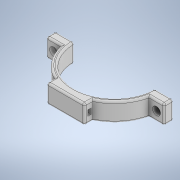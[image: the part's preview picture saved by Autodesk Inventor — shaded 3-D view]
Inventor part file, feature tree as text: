
AUTODESK INVENTOR PART (.ipt)
format: ipt  version: 2020 (Build 240168000, 168)  size: 262,656 bytes
history: native  units: in
note: dims shown in document units (in); Inventor stores cm internally (conversion verified against a paired STEP export)
features: sketch x6, extrude x5, plane x2, mirror x2, shell x1, hole x1, fillet x1, chamfer x1
ambient origin geometry x8: Origin, YZ Plane, XZ Plane, XY Plane, X Axis, Y Axis, Z Axis, Center Point
bodies: Solid1 (feature_tree)
feature tree (19):
  extrude  "Extrusion1"  Depth=0.1969in TaperAngle=0.0deg
  shell  "Shell1"  Thickness=0.1969in
  extrude  "Extrusion2"  [1 undecoded]
  plane  "Work Plane1"
  extrude  "Extrusion3"  Depth=0.3937in
  mirror  "Mirror1"
  hole  "Hole2"  [1 undecoded]
  mirror  "Mirror2"
  plane  "Work Plane2"
  extrude  "Extrusion4"  Depth=0.0984in TaperAngle=0.0deg
  fillet  "Fillet1"  Radius=0.0787in
  extrude  "Extrusion6"  Depth=0.0984in
  chamfer  "Chamfer2"  Distance=0.1969in
  sketch  "Sketch1"  dims[d0=3.7402in d1=0.7874in d2=0.0in d3=0.1969in]
  sketch  "Sketch2"  dims[d4=0.3937in d5=0.0in d6=-1.8701in]
  sketch  "Sketch3"  dims[d7=0.7874in d8=0.3937in]
  sketch  "Sketch5"  dims[d9=0.0787in d10=0.5906in d11=0.0in d12=0.0in]
  sketch  "Sketch6"  dims[d20=0.2165in d21=0.2362in d22=0.3346in d23=0.1969in d24=90.0deg d25=0.315in d26=0.8108in d27=1.7717in]
  sketch  "Sketch10"  dims[d28=1.5748in d29=0.2756in d30=0.0984in d31=0.0in d32=0.0in d39=0.0787in d43=0.0984in d44=0.1969in d45=0.0in d46=0.0in d47=0.0197in d48=0.0787in d49=45.0deg]
note: 2 required parameter values undecoded (feature->parameter linkage not recoverable at this tier; creation-order binding heuristic only, values carry confidence <= 0.55)
